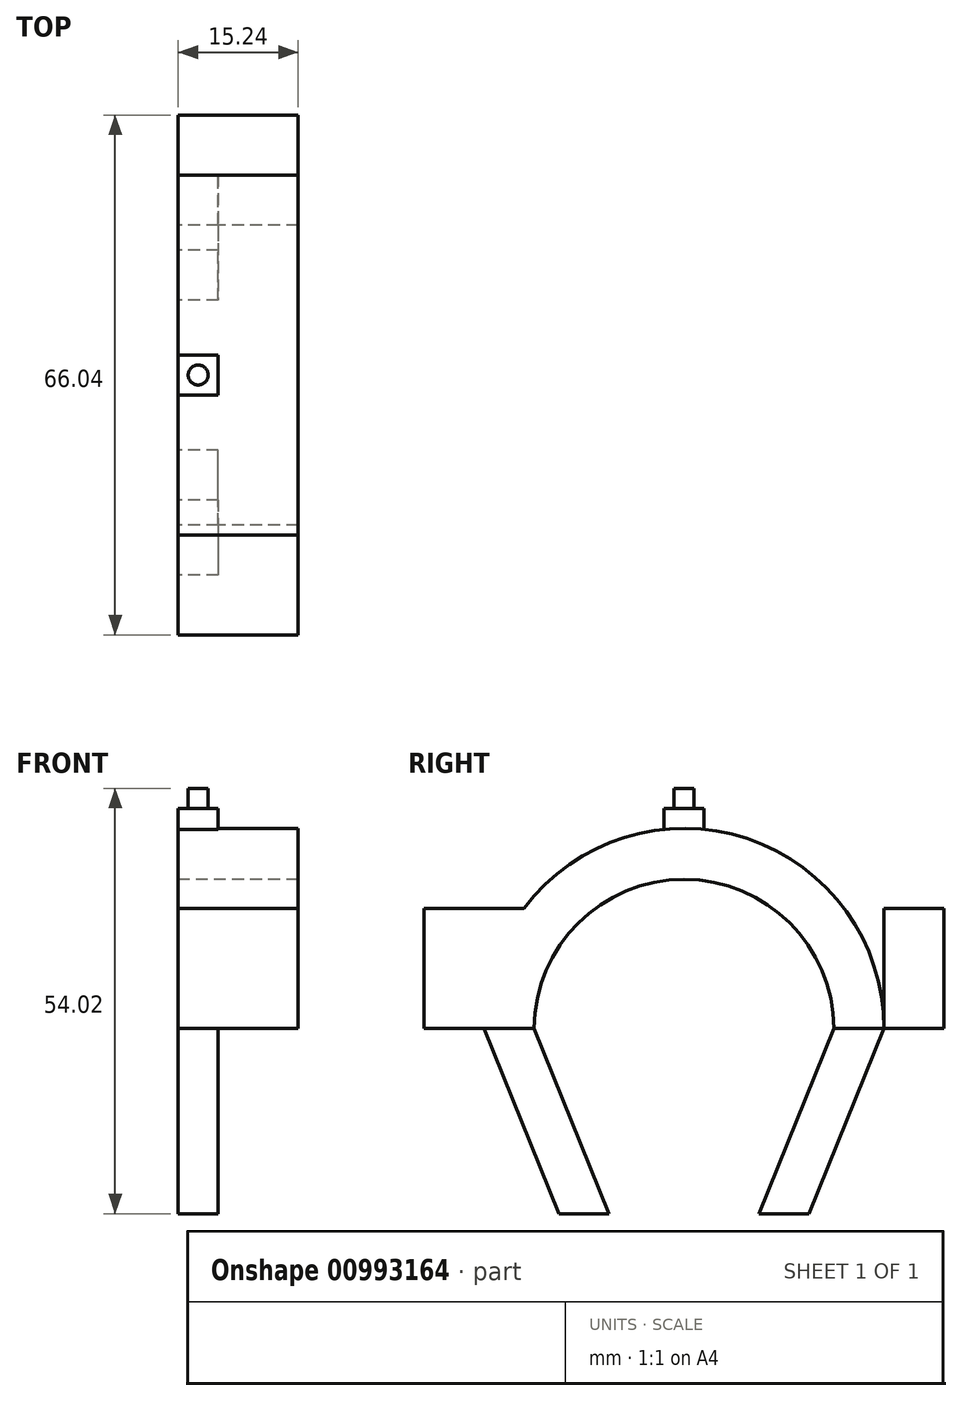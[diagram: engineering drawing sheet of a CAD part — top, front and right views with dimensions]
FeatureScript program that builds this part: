
annotation { "Feature Type Name" : "Feature", "Feature Type Description" : "" }
export const myFeature = defineFeature(function(context is Context, id is Id, definition is map)
    precondition{}
    {
        {
            var Q0;
            Q0=qCreatedBy(makeId("Right.planeOp"),FACE);
            var sketch = newSketch(context, id + "F0", { "sketchPlane" : qUnion([Q0])});
            skLineSegment(sketch, "E0", {"start": v(-48.9, 34.83) * mm, "end": v(-41.28, 34.83) * mm});
            skLineSegment(sketch, "E1", {"start": v(-31.76, 11.29) * mm, "end": v(-41.28, 34.83) * mm});
            skLineSegment(sketch, "E2", {"start": v(9.52, 34.83) * mm, "end": v(17.14, 34.83) * mm});
            skLineSegment(sketch, "E3", {"start": v(9.52, 34.83) * mm, "end": v(0, 11.29) * mm});
            skLineSegment(sketch, "E4.top", {"start": v(-48.9, 50.07) * mm, "end": v(-41.28, 50.07) * mm});
            skLineSegment(sketch, "E4.left", {"start": v(-48.9, 34.83) * mm, "end": v(-48.9, 50.07) * mm});
            skLineSegment(sketch, "E4.right", {"start": v(-41.28, 34.83) * mm, "end": v(-41.28, 50.07) * mm});
            skLineSegment(sketch, "E5.bottom", {"start": v(9.52, 50.07) * mm, "end": v(17.14, 50.07) * mm});
            skLineSegment(sketch, "E5.left", {"start": v(9.52, 50.07) * mm, "end": v(9.52, 34.83) * mm});
            skLineSegment(sketch, "E5.right", {"start": v(17.14, 50.07) * mm, "end": v(17.14, 34.83) * mm});
            skPoint(sketch, "E6.middle", {"position": v(-15.52, 61.1) * mm});
            skLineSegment(sketch, "E7.bottom", {"start": v(-13.34, 62.77) * mm, "end": v(-18.42, 62.77) * mm});
            skLineSegment(sketch, "E7.top", {"start": v(-13.34, 57.7) * mm, "end": v(-18.42, 57.7) * mm});
            skLineSegment(sketch, "E7.left", {"start": v(-13.34, 62.77) * mm, "end": v(-13.34, 57.7) * mm});
            skLineSegment(sketch, "E7.right", {"start": v(-18.42, 62.77) * mm, "end": v(-18.42, 57.7) * mm});
            skPoint(sketch, "E7.middle", {"position": v(-15.88, 60.23) * mm});
            skLineSegment(sketch, "E8", {"start": v(9.52, 50.07) * mm, "end": v(4.44, 50.07) * mm});
            skArc(sketch, "E9", {"start": v(3.17, 34.83) * mm, "mid": v(-15.88, 53.76) * mm, "end": v(-34.93, 34.83) * mm});
            skLineSegment(sketch, "E10", {"start": v(-34.93, 34.83) * mm, "end": v(-25.4, 11.29) * mm});
            skLineSegment(sketch, "E11", {"start": v(-41.28, 34.83) * mm, "end": v(-34.93, 34.83) * mm});
            skLineSegment(sketch, "E12", {"start": v(-31.76, 11.29) * mm, "end": v(-25.4, 11.29) * mm});
            skArc(sketch, "E13", {"start": v(9.52, 34.83) * mm, "mid": v(-15.88, 60.23) * mm, "end": v(-41.28, 34.83) * mm});
            skLineSegment(sketch, "E14", {"start": v(3.17, 34.83) * mm, "end": v(-6.36, 11.29) * mm});
            skLineSegment(sketch, "E15", {"start": v(-6.36, 11.29) * mm, "end": v(0, 11.29) * mm});
            skLineSegment(sketch, "E16", {"start": v(-41.28, 50.07) * mm, "end": v(-36.2, 50.07) * mm});
            skLineSegment(sketch, "E17", {"start": v(9.52, 34.83) * mm, "end": v(3.17, 34.83) * mm});
            skSolve(sketch);
        }
        {
            var Q0;
            {var subQ3=sQuery(id+"F0.wireOp",EDGE,"E3");Q0=makeQuery(id+"F0.imprint","IMPRINT",FACE,{"disambiguationData":[TD([[makeQuery(id+"F0.imprint","IMPRINT",EDGE,{"derivedFrom":subQ3}),-1.0]])]});}
            var Q1;
            {var subQ0=sQuery(id+"F0.wireOp",EDGE,"E5.left");Q1=makeQuery(id+"F0.imprint","IMPRINT",FACE,{"disambiguationData":[TD([[makeQuery(id+"F0.imprint","IMPRINT",EDGE,{"derivedFrom":subQ0}),-1.0]])]});}
            var Q2;
            Q2=makeQuery(id+"F0.imprint","IMPRINT",FACE,{"disambiguationData":[TD([[makeQuery(id+"F0.imprint","IMPRINT",EDGE,{"derivedFrom":sQuery(id+"F0.wireOp",EDGE,"E5.bottom")}),-1.0]])]});
            var Q3;
            Q3=makeQuery(id+"F0.imprint","IMPRINT",FACE,{"disambiguationData":[TD([[makeQuery(id+"F0.imprint","IMPRINT",EDGE,{"derivedFrom":sQuery(id+"F0.wireOp",EDGE,"E4.top")}),-1.0]])]});
            var Q4;
            {var subQ0=sQuery(id+"F0.wireOp",EDGE,"E4.right");Q4=makeQuery(id+"F0.imprint","IMPRINT",FACE,{"disambiguationData":[TD([[makeQuery(id+"F0.imprint","IMPRINT",EDGE,{"derivedFrom":subQ0}),-1.0]])]});}
            var Q5;
            {var subQ1=sQuery(id+"F0.wireOp",EDGE,"E1");Q5=makeQuery(id+"F0.imprint","IMPRINT",FACE,{"disambiguationData":[TD([[makeQuery(id+"F0.imprint","IMPRINT",EDGE,{"derivedFrom":subQ1}),-1.0]])]});}
            var Q6;
            {var subQ0=sQuery(id+"F0.wireOp",EDGE,"E7.top");Q6=makeQuery(id+"F0.imprint","IMPRINT",FACE,{"disambiguationData":[TD([[makeQuery(id+"F0.imprint","IMPRINT",EDGE,{"derivedFrom":subQ0}),-1.0]])]});}
            var Q7;
            {var subQ0=sQuery(id+"F0.wireOp",EDGE,"E7.bottom");Q7=makeQuery(id+"F0.imprint","IMPRINT",FACE,{"disambiguationData":[TD([[makeQuery(id+"F0.imprint","IMPRINT",EDGE,{"derivedFrom":subQ0}),1.0]])]});}
            var Q8;
            {var subQ1=sQuery(id+"F0.wireOp",EDGE,"E7.top");Q8=makeQuery(id+"F0.imprint","IMPRINT",FACE,{"disambiguationData":[TD([[makeQuery(id+"F0.imprint","IMPRINT",EDGE,{"derivedFrom":subQ1}),1.0]])]});}
            extrude(context, id + "F1", {"entities" : qUnion([Q0, Q1, Q2, Q3, Q4, Q5, Q6, Q7, Q8]), "depth" : 5.08 * mm, "offsetDistance" : 25.4 * mm});
        }
        {
            var Q0;
            Q0=makeQuery(id+"F1.opExtrude","SWEPT_FACE",FACE,{"disambiguationData":[OSD([sQuery(id+"F0.wireOp",EDGE,"E7.bottom")])]});
            var sketch = newSketch(context, id + "F2", { "sketchPlane" : qUnion([Q0])});
            skCircle(sketch, "E18", {"center": v(2.54, -15.88) * mm, "radius": 1.27 * mm});
            skPoint(sketch, "E18.centerSnap0", {"position": v(0, -15.88) * mm});
            skSolve(sketch);
        }
        {
            var Q0;
            Q0=makeQuery(id+"F2.imprint","IMPRINT",FACE,{"disambiguationData":[TD([[makeQuery(id+"F2.imprint","IMPRINT",EDGE,{"derivedFrom":sQuery(id+"F2.wireOp",EDGE,"E18")}),1.0]])]});
            extrude(context, id + "F3", {"entities" : qUnion([Q0]), "operationType" : NewBodyOperationType.ADD, "depth" : 2.54 * mm, "offsetDistance" : 25.4 * mm});
        }
        {
            var Q0;
            Q0=makeQuery(id+"F0.imprint","IMPRINT",FACE,{"disambiguationData":[TD([[makeQuery(id+"F0.imprint","IMPRINT",EDGE,{"derivedFrom":sQuery(id+"F0.wireOp",EDGE,"E4.top")}),-1.0]])]});
            var Q1;
            {var subQ0=sQuery(id+"F0.wireOp",EDGE,"E4.right");Q1=makeQuery(id+"F0.imprint","IMPRINT",FACE,{"disambiguationData":[TD([[makeQuery(id+"F0.imprint","IMPRINT",EDGE,{"derivedFrom":subQ0}),-1.0]])]});}
            var Q2;
            {var subQ1=sQuery(id+"F0.wireOp",EDGE,"E7.top");Q2=makeQuery(id+"F0.imprint","IMPRINT",FACE,{"disambiguationData":[TD([[makeQuery(id+"F0.imprint","IMPRINT",EDGE,{"derivedFrom":subQ1}),1.0]])]});}
            var Q3;
            {var subQ0=sQuery(id+"F0.wireOp",EDGE,"E5.left");Q3=makeQuery(id+"F0.imprint","IMPRINT",FACE,{"disambiguationData":[TD([[makeQuery(id+"F0.imprint","IMPRINT",EDGE,{"derivedFrom":subQ0}),-1.0]])]});}
            var Q4;
            Q4=makeQuery(id+"F0.imprint","IMPRINT",FACE,{"disambiguationData":[TD([[makeQuery(id+"F0.imprint","IMPRINT",EDGE,{"derivedFrom":sQuery(id+"F0.wireOp",EDGE,"E5.bottom")}),-1.0]])]});
            var Q5;
            {var subQ0=sQuery(id+"F0.wireOp",EDGE,"E7.top");Q5=makeQuery(id+"F0.imprint","IMPRINT",FACE,{"disambiguationData":[TD([[makeQuery(id+"F0.imprint","IMPRINT",EDGE,{"derivedFrom":subQ0}),-1.0]])]});}
            extrude(context, id + "F4", {"entities" : qUnion([Q0, Q1, Q2, Q3, Q4, Q5]), "operationType" : NewBodyOperationType.ADD, "depth" : 15.24 * mm, "offsetDistance" : 25.4 * mm});
        }
    });
